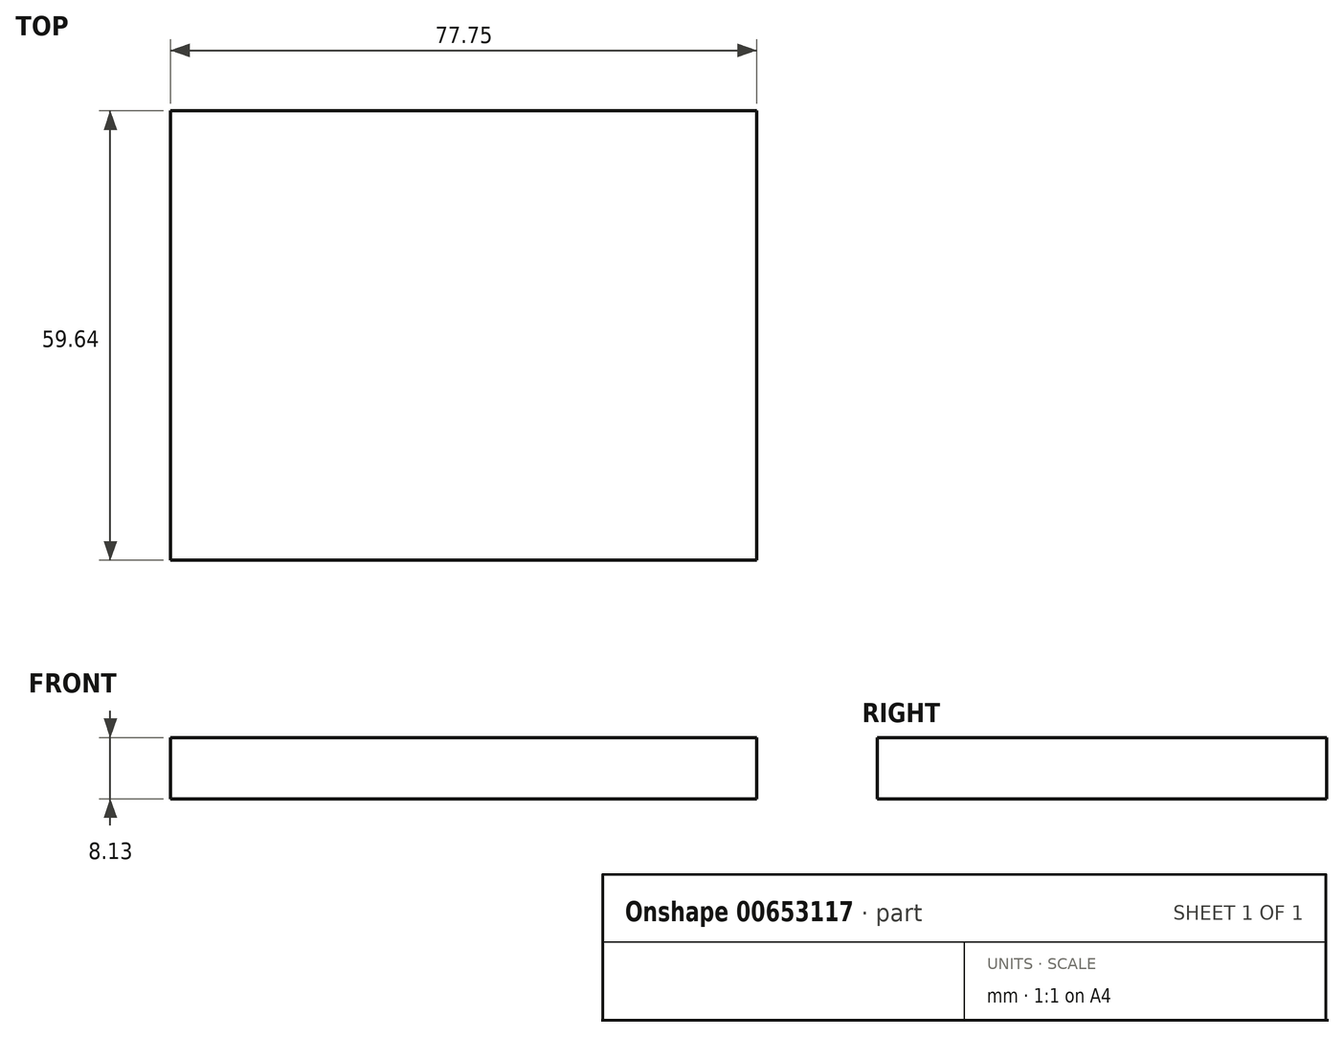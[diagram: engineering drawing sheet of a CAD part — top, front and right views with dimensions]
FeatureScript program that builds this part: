
annotation { "Feature Type Name" : "Feature", "Feature Type Description" : "" }
export const myFeature = defineFeature(function(context is Context, id is Id, definition is map)
    precondition{}
    {
        {
            var Q0;
            Q0=qCreatedBy(makeId("Top.planeOp"),FACE);
            var sketch = newSketch(context, id + "F0", { "sketchPlane" : qUnion([Q0])});
            skLineSegment(sketch, "E0.bottom", {"start": v(-54.93, 55.29) * mm, "end": v(22.82, 55.29) * mm});
            skLineSegment(sketch, "E0.top", {"start": v(-54.93, -4.35) * mm, "end": v(22.82, -4.35) * mm});
            skLineSegment(sketch, "E0.left", {"start": v(-54.93, 55.29) * mm, "end": v(-54.93, -4.35) * mm});
            skLineSegment(sketch, "E0.right", {"start": v(22.82, 55.29) * mm, "end": v(22.82, -4.35) * mm});
            skSolve(sketch);
        }
        {
            var Q0;
            Q0 = qSketchRegion(id + "F0", true);
            extrude(context, id + "F1", {"entities" : qUnion([Q0]), "depth" : 8.13 * mm, "offsetDistance" : 25.4 * mm});
        }
    });
